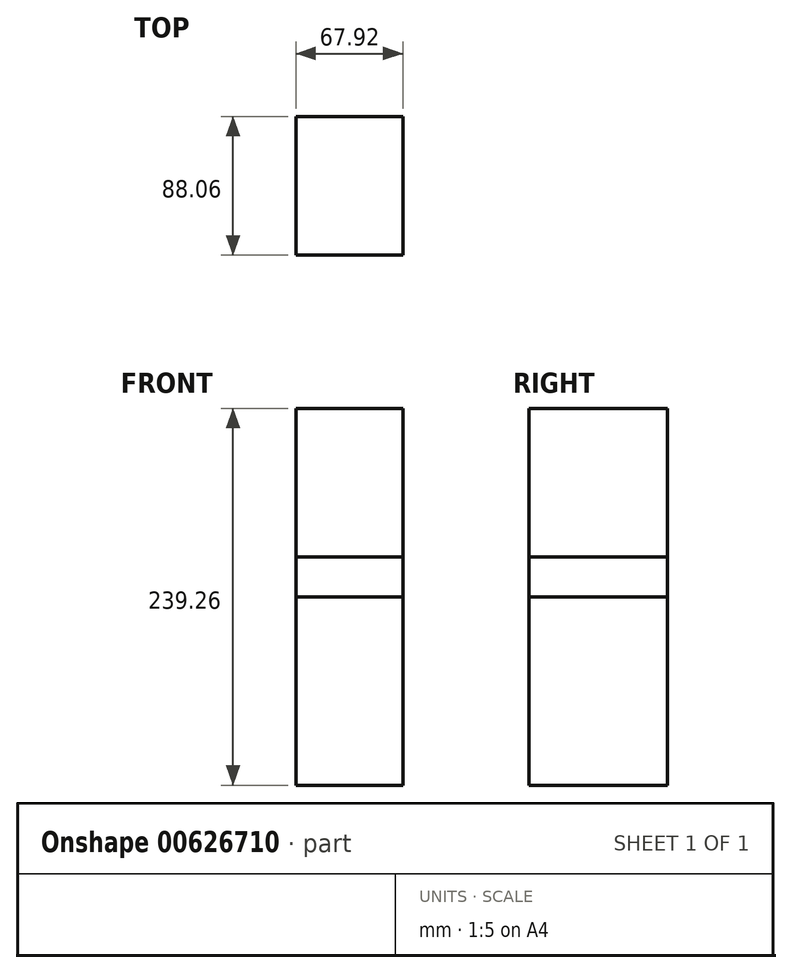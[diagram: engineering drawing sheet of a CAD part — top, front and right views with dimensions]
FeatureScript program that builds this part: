
annotation { "Feature Type Name" : "Feature", "Feature Type Description" : "" }
export const myFeature = defineFeature(function(context is Context, id is Id, definition is map)
    precondition{}
    {
        {
            var Q0;
            Q0=qCreatedBy(makeId("Top.planeOp"),FACE);
            var sketch = newSketch(context, id + "F0", { "sketchPlane" : qUnion([Q0])});
            skLineSegment(sketch, "E0.bottom", {"start": v(33.96, 44.03) * mm, "end": v(-33.96, 44.03) * mm});
            skLineSegment(sketch, "E0.top", {"start": v(33.96, -44.03) * mm, "end": v(-33.96, -44.03) * mm});
            skLineSegment(sketch, "E0.left", {"start": v(33.96, 44.03) * mm, "end": v(33.96, -44.03) * mm});
            skLineSegment(sketch, "E0.right", {"start": v(-33.96, 44.03) * mm, "end": v(-33.96, -44.03) * mm});
            skPoint(sketch, "E0.middle", {"position": v(0, 0) * mm});
            skSolve(sketch);
        }
        {
            var Q0;
            Q0=makeQuery(id+"F0.imprint","IMPRINT",FACE,{"disambiguationData":[TD([[makeQuery(id+"F0.imprint","IMPRINT",EDGE,{"derivedFrom":sQuery(id+"F0.wireOp",EDGE,"E0.bottom")}),1.0]])]});
            extrude(context, id + "F1", {"entities" : qUnion([Q0]), "depth" : 239.27 * mm, "offsetDistance" : 25.4 * mm, "symmetric" : true});
        }
        {
            var Q0;
            Q0=makeQuery(id+"F0.imprint","IMPRINT",FACE,{"disambiguationData":[TD([[makeQuery(id+"F0.imprint","IMPRINT",EDGE,{"derivedFrom":sQuery(id+"F0.wireOp",EDGE,"E0.bottom")}),1.0]])]});
            extrude(context, id + "F2", {"entities" : qUnion([Q0]), "depth" : 25.4 * mm});
        }
    });
